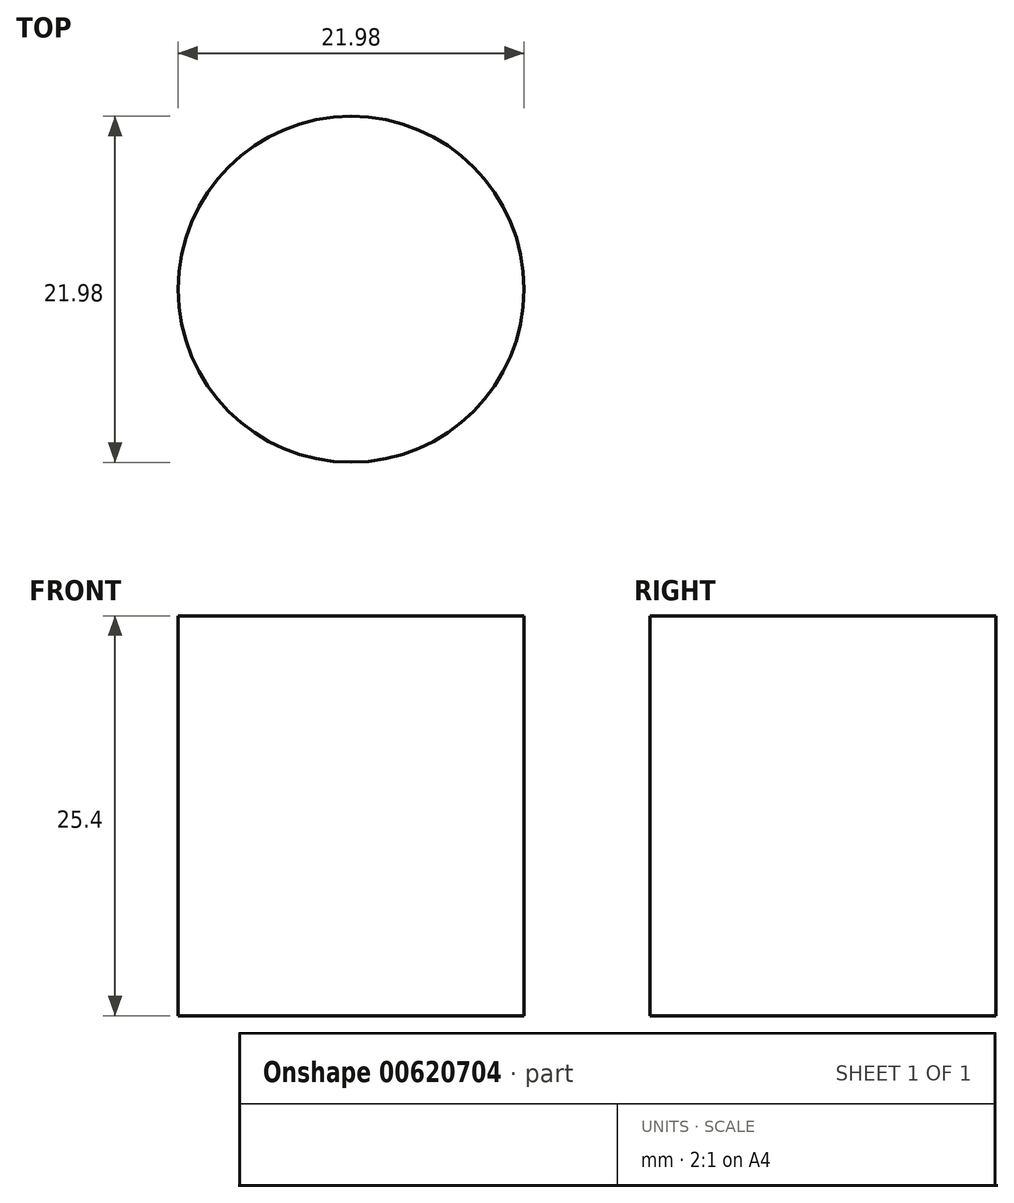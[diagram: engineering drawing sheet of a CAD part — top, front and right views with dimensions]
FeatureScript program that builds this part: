
annotation { "Feature Type Name" : "Feature", "Feature Type Description" : "" }
export const myFeature = defineFeature(function(context is Context, id is Id, definition is map)
    precondition{}
    {
        {
            var Q0;
            Q0=qCreatedBy(makeId("Top.planeOp"),FACE);
            var sketch = newSketch(context, id + "F0", { "sketchPlane" : qUnion([Q0])});
            skCircle(sketch, "E0", {"center": v(0, 0) * mm, "radius": 10.99 * mm});
            skCircle(sketch, "E1", {"center": v(37.64, 0.16) * mm, "radius": 10.99 * mm});
            skCircle(sketch, "E2", {"center": v(-38.42, 0) * mm, "radius": 11.18 * mm});
            skLineSegment(sketch, "E3", {"start": v(0, 0) * mm, "end": v(37.56, 0) * mm});
            skLineSegment(sketch, "E4", {"start": v(0, 0) * mm, "end": v(-38.42, 0) * mm});
            skCircle(sketch, "E5", {"center": v(-38.42, 0) * mm, "radius": 22.95 * mm});
            skCircle(sketch, "E6", {"center": v(37.64, 0.16) * mm, "radius": 22.6 * mm});
            skCircle(sketch, "E7", {"center": v(-38.42, 0) * mm, "radius": 15.74 * mm});
            skSolve(sketch);
        }
        {
            var Q0;
            {var subQ0=sQuery(id+"F0.wireOp",EDGE,"jmWlnDqI-k6kQ-lEwj-0NLN-aukk1m5ebamh");var subQ1=sQuery(id+"F0.wireOp",EDGE,"bMKp5jvS-M9qK-76sj-mlaE-Ndx4uhGpgFUm");var subQ2=makeQuery(id+"F0.imprint","INTERSECT",VERTEX,{"disambiguationData":[OD(0.0)],"derivedFrom":[subQ1,subQ0]});Q0=makeQuery(id+"F0.imprint","IMPRINT",FACE,{"disambiguationData":[TD([[makeQuery(id+"F0.imprint","IMPRINT",EDGE,{"disambiguationData":[TD([[subQ2,-1.0]])],"derivedFrom":subQ1}),-1.0]])]});}
            var Q1;
            {var subQ0=sQuery(id+"F0.wireOp",EDGE,"E5");var subQ1=sQuery(id+"F0.wireOp",EDGE,"E4");var subQ2=makeQuery(id+"F0.imprint","INTERSECT",VERTEX,{"derivedFrom":[subQ1,subQ0]});Q1=makeQuery(id+"F0.imprint","IMPRINT",FACE,{"disambiguationData":[TD([[makeQuery(id+"F0.imprint","IMPRINT",EDGE,{"disambiguationData":[TD([[subQ2,-1.0]])],"derivedFrom":subQ1}),1.0]])]});}
            var Q2;
            {var subQ3=sQuery(id+"F0.wireOp",EDGE,"g7RQCQqu-Aflr-wpbT-XWs8-j3dTDj1XJMci");var subQ5=sQuery(id+"F0.wireOp",EDGE,"E4");var subQ6=makeQuery(id+"F0.imprint","INTERSECT",VERTEX,{"derivedFrom":[subQ5,subQ3]});Q2=makeQuery(id+"F0.imprint","IMPRINT",FACE,{"disambiguationData":[TD([[makeQuery(id+"F0.imprint","IMPRINT",EDGE,{"disambiguationData":[TD([[subQ6,-1.0]])],"derivedFrom":subQ5}),1.0]])]});}
            var Q3;
            {var subQ0=sQuery(id+"F0.wireOp",EDGE,"E5");var subQ1=sQuery(id+"F0.wireOp",EDGE,"E4");var subQ2=makeQuery(id+"F0.imprint","INTERSECT",VERTEX,{"derivedFrom":[subQ1,subQ0]});Q3=makeQuery(id+"F0.imprint","IMPRINT",FACE,{"disambiguationData":[TD([[makeQuery(id+"F0.imprint","IMPRINT",EDGE,{"disambiguationData":[TD([[subQ2,-1.0]])],"derivedFrom":subQ1}),-1.0]])]});}
            var Q4;
            {var subQ3=sQuery(id+"F0.wireOp",EDGE,"g7RQCQqu-Aflr-wpbT-XWs8-j3dTDj1XJMci");var subQ5=sQuery(id+"F0.wireOp",EDGE,"E4");var subQ6=makeQuery(id+"F0.imprint","INTERSECT",VERTEX,{"derivedFrom":[subQ5,subQ3]});Q4=makeQuery(id+"F0.imprint","IMPRINT",FACE,{"disambiguationData":[TD([[makeQuery(id+"F0.imprint","IMPRINT",EDGE,{"disambiguationData":[TD([[subQ6,-1.0]])],"derivedFrom":subQ5}),-1.0]])]});}
            var Q5;
            {var subQ0=sQuery(id+"F0.wireOp",EDGE,"jmWlnDqI-k6kQ-lEwj-0NLN-aukk1m5ebamh");var subQ1=sQuery(id+"F0.wireOp",EDGE,"E4");var subQ2=makeQuery(id+"F0.imprint","INTERSECT",VERTEX,{"derivedFrom":[subQ1,subQ0]});Q5=makeQuery(id+"F0.imprint","IMPRINT",FACE,{"disambiguationData":[TD([[makeQuery(id+"F0.imprint","IMPRINT",EDGE,{"disambiguationData":[TD([[subQ2,1.0]])],"derivedFrom":subQ1}),1.0]])]});}
            var Q6;
            {var subQ0=sQuery(id+"F0.wireOp",EDGE,"jmWlnDqI-k6kQ-lEwj-0NLN-aukk1m5ebamh");var subQ1=sQuery(id+"F0.wireOp",EDGE,"E4");var subQ2=makeQuery(id+"F0.imprint","INTERSECT",VERTEX,{"derivedFrom":[subQ1,subQ0]});Q6=makeQuery(id+"F0.imprint","IMPRINT",FACE,{"disambiguationData":[TD([[makeQuery(id+"F0.imprint","IMPRINT",EDGE,{"disambiguationData":[TD([[subQ2,1.0]])],"derivedFrom":subQ1}),-1.0]])]});}
            var Q7;
            {var subQ0=sQuery(id+"F0.wireOp",EDGE,"E6");var subQ1=sQuery(id+"F0.wireOp",EDGE,"g7RQCQqu-Aflr-wpbT-XWs8-j3dTDj1XJMci");var subQ2=makeQuery(id+"F0.imprint","INTERSECT",VERTEX,{"disambiguationData":[OD(0.0)],"derivedFrom":[subQ1,subQ0]});Q7=makeQuery(id+"F0.imprint","IMPRINT",FACE,{"disambiguationData":[TD([[makeQuery(id+"F0.imprint","IMPRINT",EDGE,{"disambiguationData":[TD([[subQ2,-1.0]])],"derivedFrom":subQ1}),-1.0]])]});}
            var Q8;
            {var subQ0=sQuery(id+"F0.wireOp",EDGE,"E5");var subQ1=sQuery(id+"F0.wireOp",EDGE,"g7RQCQqu-Aflr-wpbT-XWs8-j3dTDj1XJMci");var subQ2=makeQuery(id+"F0.imprint","INTERSECT",VERTEX,{"disambiguationData":[OD(1.0)],"derivedFrom":[subQ1,subQ0]});Q8=makeQuery(id+"F0.imprint","IMPRINT",FACE,{"disambiguationData":[TD([[makeQuery(id+"F0.imprint","IMPRINT",EDGE,{"disambiguationData":[TD([[subQ2,-1.0]])],"derivedFrom":subQ1}),-1.0]])]});}
            var Q9;
            {var subQ0=sQuery(id+"F0.wireOp",EDGE,"g7RQCQqu-Aflr-wpbT-XWs8-j3dTDj1XJMci");var subQ1=sQuery(id+"F0.wireOp",EDGE,"sP4KQwT5-uFZq-gmgs-0oj8-Q6G9N0g5wMg1");var subQ2=makeQuery(id+"F0.imprint","INTERSECT",VERTEX,{"disambiguationData":[OD(1.0)],"derivedFrom":[subQ1,subQ0]});Q9=makeQuery(id+"F0.imprint","IMPRINT",FACE,{"disambiguationData":[TD([[makeQuery(id+"F0.imprint","IMPRINT",EDGE,{"disambiguationData":[TD([[subQ2,-1.0]])],"derivedFrom":subQ1}),-1.0]])]});}
            var Q10;
            {var subQ0=sQuery(id+"F0.wireOp",EDGE,"g7RQCQqu-Aflr-wpbT-XWs8-j3dTDj1XJMci");var subQ1=sQuery(id+"F0.wireOp",EDGE,"sP4KQwT5-uFZq-gmgs-0oj8-Q6G9N0g5wMg1");var subQ2=makeQuery(id+"F0.imprint","INTERSECT",VERTEX,{"disambiguationData":[OD(0.0)],"derivedFrom":[subQ1,subQ0]});Q10=makeQuery(id+"F0.imprint","IMPRINT",FACE,{"disambiguationData":[TD([[makeQuery(id+"F0.imprint","IMPRINT",EDGE,{"disambiguationData":[TD([[subQ2,1.0]])],"derivedFrom":subQ1}),-1.0]])]});}
            var Q11;
            {var subQ0=sQuery(id+"F0.wireOp",EDGE,"jmWlnDqI-k6kQ-lEwj-0NLN-aukk1m5ebamh");var subQ1=sQuery(id+"F0.wireOp",EDGE,"sP4KQwT5-uFZq-gmgs-0oj8-Q6G9N0g5wMg1");var subQ2=makeQuery(id+"F0.imprint","INTERSECT",VERTEX,{"disambiguationData":[OD(0.0)],"derivedFrom":[subQ1,subQ0]});Q11=makeQuery(id+"F0.imprint","IMPRINT",FACE,{"disambiguationData":[TD([[makeQuery(id+"F0.imprint","IMPRINT",EDGE,{"disambiguationData":[TD([[subQ2,1.0]])],"derivedFrom":subQ1}),-1.0]])]});}
            var Q12;
            {var subQ0=sQuery(id+"F0.wireOp",EDGE,"E6");var subQ1=sQuery(id+"F0.wireOp",EDGE,"E3");var subQ2=makeQuery(id+"F0.imprint","INTERSECT",VERTEX,{"derivedFrom":[subQ1,subQ0]});Q12=makeQuery(id+"F0.imprint","IMPRINT",FACE,{"disambiguationData":[TD([[makeQuery(id+"F0.imprint","IMPRINT",EDGE,{"disambiguationData":[TD([[subQ2,-1.0]])],"derivedFrom":subQ1}),-1.0]])]});}
            var Q13;
            {var subQ0=sQuery(id+"F0.wireOp",EDGE,"E6");var subQ1=sQuery(id+"F0.wireOp",EDGE,"E3");var subQ2=makeQuery(id+"F0.imprint","INTERSECT",VERTEX,{"derivedFrom":[subQ1,subQ0]});Q13=makeQuery(id+"F0.imprint","IMPRINT",FACE,{"disambiguationData":[TD([[makeQuery(id+"F0.imprint","IMPRINT",EDGE,{"disambiguationData":[TD([[subQ2,-1.0]])],"derivedFrom":subQ1}),1.0]])]});}
            var Q14;
            {var subQ0=sQuery(id+"F0.wireOp",EDGE,"E3");var subQ1=sQuery(id+"F0.wireOp",EDGE,"E0");var subQ2=makeQuery(id+"F0.imprint","INTERSECT",VERTEX,{"derivedFrom":[subQ1,subQ0]});Q14=makeQuery(id+"F0.imprint","IMPRINT",FACE,{"disambiguationData":[TD([[makeQuery(id+"F0.imprint","IMPRINT",EDGE,{"disambiguationData":[TD([[subQ2,1.0]])],"derivedFrom":subQ1}),1.0]])]});}
            var Q15;
            {var subQ0=sQuery(id+"F0.wireOp",EDGE,"jmWlnDqI-k6kQ-lEwj-0NLN-aukk1m5ebamh");var subQ1=sQuery(id+"F0.wireOp",EDGE,"E3");var subQ2=makeQuery(id+"F0.imprint","INTERSECT",VERTEX,{"derivedFrom":[subQ1,subQ0]});Q15=makeQuery(id+"F0.imprint","IMPRINT",FACE,{"disambiguationData":[TD([[makeQuery(id+"F0.imprint","IMPRINT",EDGE,{"disambiguationData":[TD([[subQ2,1.0]])],"derivedFrom":subQ1}),1.0]])]});}
            var Q16;
            {var subQ0=sQuery(id+"F0.wireOp",EDGE,"jmWlnDqI-k6kQ-lEwj-0NLN-aukk1m5ebamh");var subQ1=sQuery(id+"F0.wireOp",EDGE,"E3");var subQ2=makeQuery(id+"F0.imprint","INTERSECT",VERTEX,{"derivedFrom":[subQ1,subQ0]});Q16=makeQuery(id+"F0.imprint","IMPRINT",FACE,{"disambiguationData":[TD([[makeQuery(id+"F0.imprint","IMPRINT",EDGE,{"disambiguationData":[TD([[subQ2,1.0]])],"derivedFrom":subQ1}),-1.0]])]});}
            var Q17;
            {var subQ5=sQuery(id+"F0.wireOp",EDGE,"E3");var subQ6=sQuery(id+"F0.wireOp",EDGE,"E0");var subQ7=makeQuery(id+"F0.imprint","INTERSECT",VERTEX,{"derivedFrom":[subQ6,subQ5]});Q17=makeQuery(id+"F0.imprint","IMPRINT",FACE,{"disambiguationData":[TD([[makeQuery(id+"F0.imprint","IMPRINT",EDGE,{"disambiguationData":[TD([[subQ7,1.0]])],"derivedFrom":subQ6}),-1.0]])]});}
            var Q18;
            {var subQ0=sQuery(id+"F0.wireOp",EDGE,"E3");var subQ1=sQuery(id+"F0.wireOp",EDGE,"E0");var subQ2=makeQuery(id+"F0.imprint","INTERSECT",VERTEX,{"derivedFrom":[subQ1,subQ0]});Q18=makeQuery(id+"F0.imprint","IMPRINT",FACE,{"disambiguationData":[TD([[makeQuery(id+"F0.imprint","IMPRINT",EDGE,{"disambiguationData":[TD([[subQ2,-1.0]])],"derivedFrom":subQ1}),1.0]])]});}
            var Q19;
            {var subQ5=sQuery(id+"F0.wireOp",EDGE,"E3");var subQ8=sQuery(id+"F0.wireOp",EDGE,"E0");var subQ11=makeQuery(id+"F0.imprint","INTERSECT",VERTEX,{"derivedFrom":[subQ8,subQ5]});Q19=makeQuery(id+"F0.imprint","IMPRINT",FACE,{"disambiguationData":[TD([[makeQuery(id+"F0.imprint","IMPRINT",EDGE,{"disambiguationData":[TD([[subQ11,-1.0]])],"derivedFrom":subQ8}),-1.0]])]});}
            var Q20;
            {var subQ0=sQuery(id+"F0.wireOp",EDGE,"jmWlnDqI-k6kQ-lEwj-0NLN-aukk1m5ebamh");var subQ1=sQuery(id+"F0.wireOp",EDGE,"bMKp5jvS-M9qK-76sj-mlaE-Ndx4uhGpgFUm");var subQ2=makeQuery(id+"F0.imprint","INTERSECT",VERTEX,{"disambiguationData":[OD(0.0)],"derivedFrom":[subQ1,subQ0]});Q20=makeQuery(id+"F0.imprint","IMPRINT",FACE,{"disambiguationData":[TD([[makeQuery(id+"F0.imprint","IMPRINT",EDGE,{"disambiguationData":[TD([[subQ2,-1.0]])],"derivedFrom":subQ1}),1.0]])]});}
            var Q21;
            {var subQ0=sQuery(id+"F0.wireOp",EDGE,"bMKp5jvS-M9qK-76sj-mlaE-Ndx4uhGpgFUm");var subQ1=sQuery(id+"F0.wireOp",EDGE,"E4");var subQ2=makeQuery(id+"F0.imprint","INTERSECT",VERTEX,{"derivedFrom":[subQ1,subQ0]});Q21=makeQuery(id+"F0.imprint","IMPRINT",FACE,{"disambiguationData":[TD([[makeQuery(id+"F0.imprint","IMPRINT",EDGE,{"disambiguationData":[TD([[subQ2,-1.0]])],"derivedFrom":subQ1}),1.0]])]});}
            var Q22;
            {var subQ0=sQuery(id+"F0.wireOp",EDGE,"bMKp5jvS-M9qK-76sj-mlaE-Ndx4uhGpgFUm");var subQ1=sQuery(id+"F0.wireOp",EDGE,"E4");var subQ2=makeQuery(id+"F0.imprint","INTERSECT",VERTEX,{"derivedFrom":[subQ1,subQ0]});Q22=makeQuery(id+"F0.imprint","IMPRINT",FACE,{"disambiguationData":[TD([[makeQuery(id+"F0.imprint","IMPRINT",EDGE,{"disambiguationData":[TD([[subQ2,-1.0]])],"derivedFrom":subQ1}),-1.0]])]});}
            var Q23;
            {var subQ0=sQuery(id+"F0.wireOp",EDGE,"jmWlnDqI-k6kQ-lEwj-0NLN-aukk1m5ebamh");var subQ1=sQuery(id+"F0.wireOp",EDGE,"sP4KQwT5-uFZq-gmgs-0oj8-Q6G9N0g5wMg1");var subQ2=makeQuery(id+"F0.imprint","INTERSECT",VERTEX,{"disambiguationData":[OD(0.0)],"derivedFrom":[subQ1,subQ0]});Q23=makeQuery(id+"F0.imprint","IMPRINT",FACE,{"disambiguationData":[TD([[makeQuery(id+"F0.imprint","IMPRINT",EDGE,{"disambiguationData":[TD([[subQ2,1.0]])],"derivedFrom":subQ1}),1.0]])]});}
            var Q24;
            {var subQ0=sQuery(id+"F0.wireOp",EDGE,"g7RQCQqu-Aflr-wpbT-XWs8-j3dTDj1XJMci");var subQ1=sQuery(id+"F0.wireOp",EDGE,"E3");var subQ2=makeQuery(id+"F0.imprint","INTERSECT",VERTEX,{"derivedFrom":[subQ1,subQ0]});Q24=makeQuery(id+"F0.imprint","IMPRINT",FACE,{"disambiguationData":[TD([[makeQuery(id+"F0.imprint","IMPRINT",EDGE,{"disambiguationData":[TD([[subQ2,-1.0]])],"derivedFrom":subQ1}),1.0]])]});}
            var Q25;
            {var subQ5=sQuery(id+"F0.wireOp",EDGE,"E3");var subQ7=sQuery(id+"F0.wireOp",EDGE,"g7RQCQqu-Aflr-wpbT-XWs8-j3dTDj1XJMci");var subQ8=makeQuery(id+"F0.imprint","INTERSECT",VERTEX,{"derivedFrom":[subQ5,subQ7]});Q25=makeQuery(id+"F0.imprint","IMPRINT",FACE,{"disambiguationData":[TD([[makeQuery(id+"F0.imprint","IMPRINT",EDGE,{"disambiguationData":[TD([[subQ8,-1.0]])],"derivedFrom":subQ5}),-1.0]])]});}
            extrude(context, id + "F1", {"entities" : qUnion([Q0, Q1, Q2, Q3, Q4, Q5, Q6, Q7, Q8, Q9, Q10, Q11, Q12, Q13, Q14, Q15, Q16, Q17, Q18, Q19, Q20, Q21, Q22, Q23, Q24, Q25]), "depth" : 25.4 * mm, "offsetDistance" : 25.4 * mm});
        }
    });
